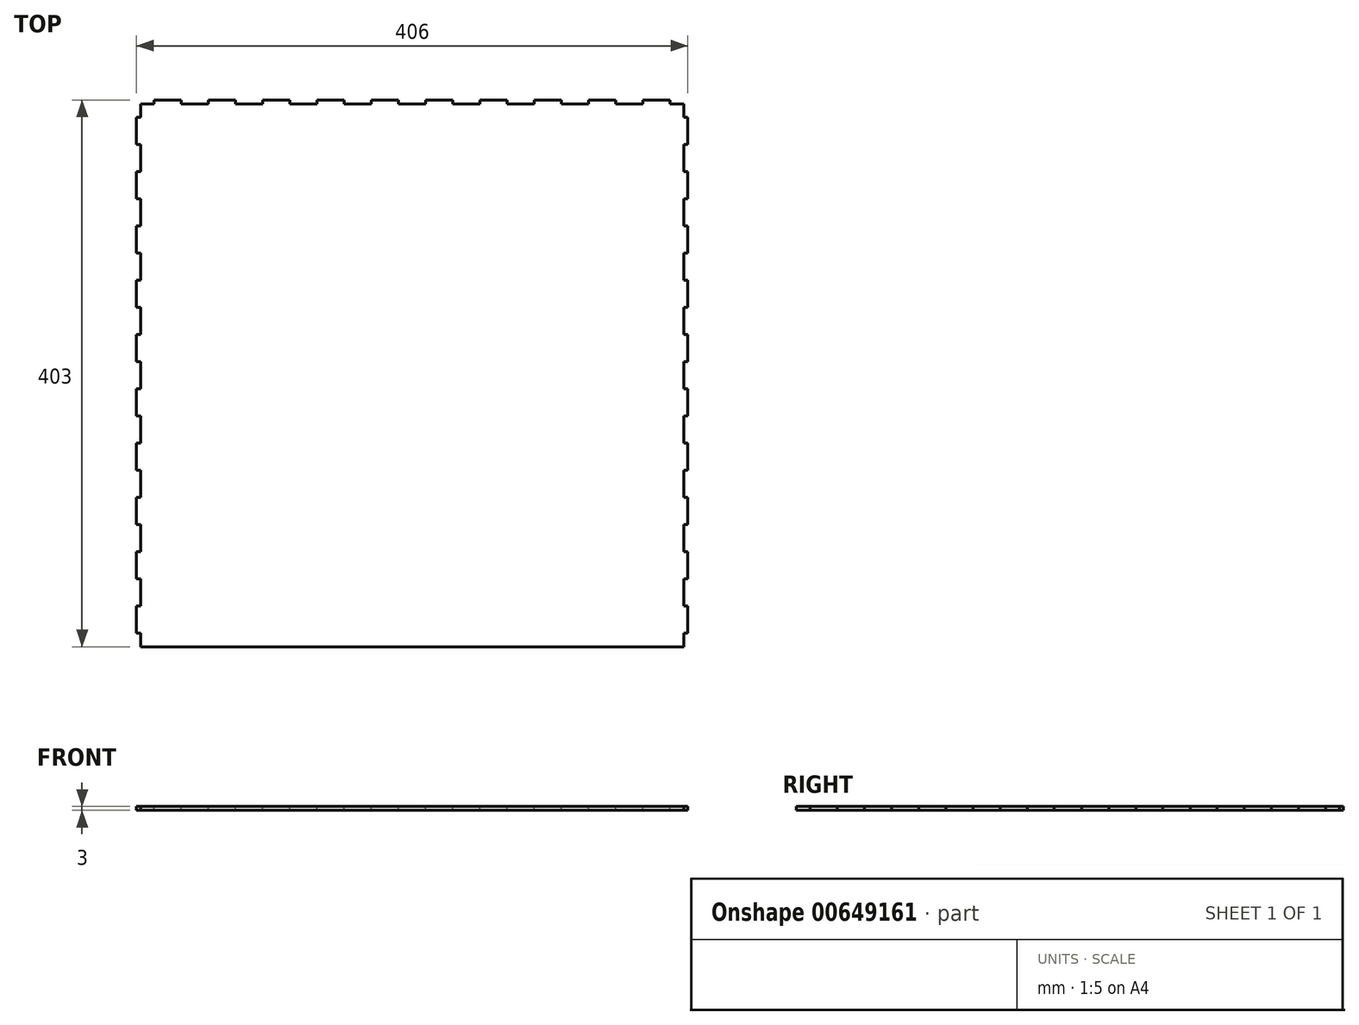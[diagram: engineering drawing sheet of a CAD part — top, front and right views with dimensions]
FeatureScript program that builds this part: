
annotation { "Feature Type Name" : "Feature", "Feature Type Description" : "" }
export const myFeature = defineFeature(function(context is Context, id is Id, definition is map)
    precondition{}
    {
        {
            var Q0;
            Q0=qCreatedBy(makeId("Top.planeOp"),FACE);
            var sketch = newSketch(context, id + "F0", { "sketchPlane" : qUnion([Q0])});
            skLineSegment(sketch, "E0.bottom", {"start": v(200, -200) * mm, "end": v(-200, -200) * mm});
            skLineSegment(sketch, "E0.top", {"start": v(200, 200) * mm, "end": v(-200, 200) * mm});
            skLineSegment(sketch, "E0.left", {"start": v(200, -200) * mm, "end": v(200, 200) * mm});
            skLineSegment(sketch, "E0.right", {"start": v(-200, -200) * mm, "end": v(-200, 200) * mm});
            skPoint(sketch, "E0.middle", {"position": v(0, 0) * mm});
            skSolve(sketch);
        }
        {
            var Q0;
            Q0=makeQuery(id+"F0.imprint","IMPRINT",FACE,{"disambiguationData":[TD([[makeQuery(id+"F0.imprint","IMPRINT",EDGE,{"derivedFrom":sQuery(id+"F0.wireOp",EDGE,"E0.bottom")}),-1.0]])]});
            extrude(context, id + "F1", {"entities" : qUnion([Q0]), "depth" : 3 * mm, "offsetDistance" : 25 * mm});
        }
        {
            var Q0;
            Q0=makeQuery(id+"F1.opExtrude","CAP_FACE",FACE,{"disambiguationData":[OSD([sQuery(id+"F0.wireOp",EDGE,"E0.bottom"),sQuery(id+"F0.wireOp",EDGE,"E0.top"),sQuery(id+"F0.wireOp",EDGE,"E0.left"),sQuery(id+"F0.wireOp",EDGE,"E0.right")])],"isStart":false});
            var sketch = newSketch(context, id + "F2", { "sketchPlane" : qUnion([Q0])});
            skLineSegment(sketch, "E1", {"start": v(-200, -200) * mm, "end": v(-190, -200) * mm, "construction": true});
            skLineSegment(sketch, "E2.bottom", {"start": v(-190, -200) * mm, "end": v(-170, -200) * mm});
            skLineSegment(sketch, "E2.top", {"start": v(-190, -203) * mm, "end": v(-170, -203) * mm});
            skLineSegment(sketch, "E2.left", {"start": v(-190, -200) * mm, "end": v(-190, -203) * mm});
            skLineSegment(sketch, "E2.right", {"start": v(-170, -200) * mm, "end": v(-170, -203) * mm});
            skLineSegment(sketch, "E3.1.0.0", {"start": v(-150, -200) * mm, "end": v(-150, -203) * mm});
            skLineSegment(sketch, "E3.1.0.1", {"start": v(-150, -200) * mm, "end": v(-130, -200) * mm});
            skLineSegment(sketch, "E3.1.0.2", {"start": v(-150, -203) * mm, "end": v(-130, -203) * mm});
            skLineSegment(sketch, "E3.1.0.3", {"start": v(-130, -200) * mm, "end": v(-130, -203) * mm});
            skLineSegment(sketch, "E3.2.0.0", {"start": v(-110, -200) * mm, "end": v(-110, -203) * mm});
            skLineSegment(sketch, "E3.2.0.1", {"start": v(-110, -200) * mm, "end": v(-90, -200) * mm});
            skLineSegment(sketch, "E3.2.0.2", {"start": v(-110, -203) * mm, "end": v(-90, -203) * mm});
            skLineSegment(sketch, "E3.2.0.3", {"start": v(-90, -200) * mm, "end": v(-90, -203) * mm});
            skLineSegment(sketch, "E3.3.0.0", {"start": v(-70, -200) * mm, "end": v(-70, -203) * mm});
            skLineSegment(sketch, "E3.3.0.1", {"start": v(-70, -200) * mm, "end": v(-50, -200) * mm});
            skLineSegment(sketch, "E3.3.0.2", {"start": v(-70, -203) * mm, "end": v(-50, -203) * mm});
            skLineSegment(sketch, "E3.3.0.3", {"start": v(-50, -200) * mm, "end": v(-50, -203) * mm});
            skLineSegment(sketch, "E3.4.0.0", {"start": v(-30, -200) * mm, "end": v(-30, -203) * mm});
            skLineSegment(sketch, "E3.4.0.1", {"start": v(-30, -200) * mm, "end": v(-10, -200) * mm});
            skLineSegment(sketch, "E3.4.0.2", {"start": v(-30, -203) * mm, "end": v(-10, -203) * mm});
            skLineSegment(sketch, "E3.4.0.3", {"start": v(-10, -200) * mm, "end": v(-10, -203) * mm});
            skLineSegment(sketch, "E3.5.0.0", {"start": v(10, -200) * mm, "end": v(10, -203) * mm});
            skLineSegment(sketch, "E3.5.0.1", {"start": v(10, -200) * mm, "end": v(30, -200) * mm});
            skLineSegment(sketch, "E3.5.0.2", {"start": v(10, -203) * mm, "end": v(30, -203) * mm});
            skLineSegment(sketch, "E3.5.0.3", {"start": v(30, -200) * mm, "end": v(30, -203) * mm});
            skLineSegment(sketch, "E3.6.0.0", {"start": v(50, -200) * mm, "end": v(50, -203) * mm});
            skLineSegment(sketch, "E3.6.0.1", {"start": v(50, -200) * mm, "end": v(70, -200) * mm});
            skLineSegment(sketch, "E3.6.0.2", {"start": v(50, -203) * mm, "end": v(70, -203) * mm});
            skLineSegment(sketch, "E3.6.0.3", {"start": v(70, -200) * mm, "end": v(70, -203) * mm});
            skLineSegment(sketch, "E3.7.0.0", {"start": v(90, -200) * mm, "end": v(90, -203) * mm});
            skLineSegment(sketch, "E3.7.0.1", {"start": v(90, -200) * mm, "end": v(110, -200) * mm});
            skLineSegment(sketch, "E3.7.0.2", {"start": v(90, -203) * mm, "end": v(110, -203) * mm});
            skLineSegment(sketch, "E3.7.0.3", {"start": v(110, -200) * mm, "end": v(110, -203) * mm});
            skLineSegment(sketch, "E3.8.0.0", {"start": v(130, -200) * mm, "end": v(130, -203) * mm});
            skLineSegment(sketch, "E3.8.0.1", {"start": v(130, -200) * mm, "end": v(150, -200) * mm});
            skLineSegment(sketch, "E3.8.0.2", {"start": v(130, -203) * mm, "end": v(150, -203) * mm});
            skLineSegment(sketch, "E3.8.0.3", {"start": v(150, -200) * mm, "end": v(150, -203) * mm});
            skLineSegment(sketch, "E3.9.0.0", {"start": v(170, -200) * mm, "end": v(170, -203) * mm});
            skLineSegment(sketch, "E3.9.0.1", {"start": v(170, -200) * mm, "end": v(190, -200) * mm});
            skLineSegment(sketch, "E3.9.0.2", {"start": v(170, -203) * mm, "end": v(190, -203) * mm});
            skLineSegment(sketch, "E3.9.0.3", {"start": v(190, -200) * mm, "end": v(190, -203) * mm});
            skLineSegment(sketch, "E3.direction1", {"start": v(-190, -203) * mm, "end": v(-150, -203) * mm, "construction": true});
            skLineSegment(sketch, "E4.1.0", {"start": v(200, 90) * mm, "end": v(200, 110) * mm});
            skLineSegment(sketch, "E4.1.1", {"start": v(200, 170) * mm, "end": v(203, 170) * mm});
            skLineSegment(sketch, "E4.1.2", {"start": v(200, 10) * mm, "end": v(203, 10) * mm});
            skLineSegment(sketch, "E4.1.3", {"start": v(200, 130) * mm, "end": v(203, 130) * mm});
            skLineSegment(sketch, "E4.1.4", {"start": v(200, -30) * mm, "end": v(203, -30) * mm});
            skLineSegment(sketch, "E4.1.5", {"start": v(203, -190) * mm, "end": v(203, -150) * mm, "construction": true});
            skLineSegment(sketch, "E4.1.6", {"start": v(200, 170) * mm, "end": v(200, 190) * mm});
            skLineSegment(sketch, "E4.1.7", {"start": v(203, 90) * mm, "end": v(203, 110) * mm});
            skLineSegment(sketch, "E4.1.8", {"start": v(200, 10) * mm, "end": v(200, 30) * mm});
            skLineSegment(sketch, "E4.1.9", {"start": v(200, 130) * mm, "end": v(200, 150) * mm});
            skLineSegment(sketch, "E4.1.10", {"start": v(200, -30) * mm, "end": v(200, -10) * mm});
            skLineSegment(sketch, "E4.1.11", {"start": v(200, 50) * mm, "end": v(200, 70) * mm});
            skLineSegment(sketch, "E4.1.12", {"start": v(200, -70) * mm, "end": v(200, -50) * mm});
            skLineSegment(sketch, "E4.1.13", {"start": v(203, -70) * mm, "end": v(203, -50) * mm});
            skLineSegment(sketch, "E4.1.14", {"start": v(200, -190) * mm, "end": v(200, -170) * mm});
            skLineSegment(sketch, "E4.1.15", {"start": v(200, -170) * mm, "end": v(203, -170) * mm});
            skLineSegment(sketch, "E4.1.16", {"start": v(203, 130) * mm, "end": v(203, 150) * mm});
            skLineSegment(sketch, "E4.1.17", {"start": v(203, -30) * mm, "end": v(203, -10) * mm});
            skLineSegment(sketch, "E4.1.18", {"start": v(200, -150) * mm, "end": v(200, -130) * mm});
            skLineSegment(sketch, "E4.1.19", {"start": v(203, -150) * mm, "end": v(203, -130) * mm});
            skLineSegment(sketch, "E4.1.20", {"start": v(200, -130) * mm, "end": v(203, -130) * mm});
            skLineSegment(sketch, "E4.1.21", {"start": v(200, -110) * mm, "end": v(200, -90) * mm});
            skLineSegment(sketch, "E4.1.22", {"start": v(203, -110) * mm, "end": v(203, -90) * mm});
            skLineSegment(sketch, "E4.1.23", {"start": v(200, -90) * mm, "end": v(203, -90) * mm});
            skLineSegment(sketch, "E4.1.24", {"start": v(200, 110) * mm, "end": v(203, 110) * mm});
            skLineSegment(sketch, "E4.1.25", {"start": v(200, -50) * mm, "end": v(203, -50) * mm});
            skLineSegment(sketch, "E4.1.26", {"start": v(203, 50) * mm, "end": v(203, 70) * mm});
            skLineSegment(sketch, "E4.1.27", {"start": v(203, 170) * mm, "end": v(203, 190) * mm});
            skLineSegment(sketch, "E4.1.28", {"start": v(203, 10) * mm, "end": v(203, 30) * mm});
            skLineSegment(sketch, "E4.1.29", {"start": v(200, 150) * mm, "end": v(203, 150) * mm});
            skLineSegment(sketch, "E4.1.30", {"start": v(200, -10) * mm, "end": v(203, -10) * mm});
            skLineSegment(sketch, "E4.1.31", {"start": v(200, 90) * mm, "end": v(203, 90) * mm});
            skLineSegment(sketch, "E4.1.32", {"start": v(200, 70) * mm, "end": v(203, 70) * mm});
            skLineSegment(sketch, "E4.1.33", {"start": v(200, 190) * mm, "end": v(203, 190) * mm});
            skLineSegment(sketch, "E4.1.34", {"start": v(200, 30) * mm, "end": v(203, 30) * mm});
            skLineSegment(sketch, "E4.1.35", {"start": v(200, 50) * mm, "end": v(203, 50) * mm});
            skLineSegment(sketch, "E4.1.36", {"start": v(200, -70) * mm, "end": v(203, -70) * mm});
            skLineSegment(sketch, "E4.1.37", {"start": v(203, -190) * mm, "end": v(203, -170) * mm});
            skLineSegment(sketch, "E4.1.38", {"start": v(200, -150) * mm, "end": v(203, -150) * mm});
            skLineSegment(sketch, "E4.1.39", {"start": v(200, -110) * mm, "end": v(203, -110) * mm});
            skLineSegment(sketch, "E4.1.40", {"start": v(200, -200) * mm, "end": v(200, -190) * mm, "construction": true});
            skLineSegment(sketch, "E4.1.41", {"start": v(200, -190) * mm, "end": v(203, -190) * mm});
            skLineSegment(sketch, "E4.2.0", {"start": v(-90, 200) * mm, "end": v(-110, 200) * mm});
            skLineSegment(sketch, "E4.2.1", {"start": v(-170, 200) * mm, "end": v(-170, 203) * mm});
            skLineSegment(sketch, "E4.2.2", {"start": v(-10, 200) * mm, "end": v(-10, 203) * mm});
            skLineSegment(sketch, "E4.2.3", {"start": v(-130, 200) * mm, "end": v(-130, 203) * mm});
            skLineSegment(sketch, "E4.2.4", {"start": v(30, 200) * mm, "end": v(30, 203) * mm});
            skLineSegment(sketch, "E4.2.5", {"start": v(190, 203) * mm, "end": v(150, 203) * mm, "construction": true});
            skLineSegment(sketch, "E4.2.6", {"start": v(-170, 200) * mm, "end": v(-190, 200) * mm});
            skLineSegment(sketch, "E4.2.7", {"start": v(-90, 203) * mm, "end": v(-110, 203) * mm});
            skLineSegment(sketch, "E4.2.8", {"start": v(-10, 200) * mm, "end": v(-30, 200) * mm});
            skLineSegment(sketch, "E4.2.9", {"start": v(-130, 200) * mm, "end": v(-150, 200) * mm});
            skLineSegment(sketch, "E4.2.10", {"start": v(30, 200) * mm, "end": v(10, 200) * mm});
            skLineSegment(sketch, "E4.2.11", {"start": v(-50, 200) * mm, "end": v(-70, 200) * mm});
            skLineSegment(sketch, "E4.2.12", {"start": v(70, 200) * mm, "end": v(50, 200) * mm});
            skLineSegment(sketch, "E4.2.13", {"start": v(70, 203) * mm, "end": v(50, 203) * mm});
            skLineSegment(sketch, "E4.2.14", {"start": v(190, 200) * mm, "end": v(170, 200) * mm});
            skLineSegment(sketch, "E4.2.15", {"start": v(170, 200) * mm, "end": v(170, 203) * mm});
            skLineSegment(sketch, "E4.2.16", {"start": v(-130, 203) * mm, "end": v(-150, 203) * mm});
            skLineSegment(sketch, "E4.2.17", {"start": v(30, 203) * mm, "end": v(10, 203) * mm});
            skLineSegment(sketch, "E4.2.18", {"start": v(150, 200) * mm, "end": v(130, 200) * mm});
            skLineSegment(sketch, "E4.2.19", {"start": v(150, 203) * mm, "end": v(130, 203) * mm});
            skLineSegment(sketch, "E4.2.20", {"start": v(130, 200) * mm, "end": v(130, 203) * mm});
            skLineSegment(sketch, "E4.2.21", {"start": v(110, 200) * mm, "end": v(90, 200) * mm});
            skLineSegment(sketch, "E4.2.22", {"start": v(110, 203) * mm, "end": v(90, 203) * mm});
            skLineSegment(sketch, "E4.2.23", {"start": v(90, 200) * mm, "end": v(90, 203) * mm});
            skLineSegment(sketch, "E4.2.24", {"start": v(-110, 200) * mm, "end": v(-110, 203) * mm});
            skLineSegment(sketch, "E4.2.25", {"start": v(50, 200) * mm, "end": v(50, 203) * mm});
            skLineSegment(sketch, "E4.2.26", {"start": v(-50, 203) * mm, "end": v(-70, 203) * mm});
            skLineSegment(sketch, "E4.2.27", {"start": v(-170, 203) * mm, "end": v(-190, 203) * mm});
            skLineSegment(sketch, "E4.2.28", {"start": v(-10, 203) * mm, "end": v(-30, 203) * mm});
            skLineSegment(sketch, "E4.2.29", {"start": v(-150, 200) * mm, "end": v(-150, 203) * mm});
            skLineSegment(sketch, "E4.2.30", {"start": v(10, 200) * mm, "end": v(10, 203) * mm});
            skLineSegment(sketch, "E4.2.31", {"start": v(-90, 200) * mm, "end": v(-90, 203) * mm});
            skLineSegment(sketch, "E4.2.32", {"start": v(-70, 200) * mm, "end": v(-70, 203) * mm});
            skLineSegment(sketch, "E4.2.33", {"start": v(-190, 200) * mm, "end": v(-190, 203) * mm});
            skLineSegment(sketch, "E4.2.34", {"start": v(-30, 200) * mm, "end": v(-30, 203) * mm});
            skLineSegment(sketch, "E4.2.35", {"start": v(-50, 200) * mm, "end": v(-50, 203) * mm});
            skLineSegment(sketch, "E4.2.36", {"start": v(70, 200) * mm, "end": v(70, 203) * mm});
            skLineSegment(sketch, "E4.2.37", {"start": v(190, 203) * mm, "end": v(170, 203) * mm});
            skLineSegment(sketch, "E4.2.38", {"start": v(150, 200) * mm, "end": v(150, 203) * mm});
            skLineSegment(sketch, "E4.2.39", {"start": v(110, 200) * mm, "end": v(110, 203) * mm});
            skLineSegment(sketch, "E4.2.40", {"start": v(200, 200) * mm, "end": v(190, 200) * mm, "construction": true});
            skLineSegment(sketch, "E4.2.41", {"start": v(190, 200) * mm, "end": v(190, 203) * mm});
            skLineSegment(sketch, "E4.3.0", {"start": v(-200, -90) * mm, "end": v(-200, -110) * mm});
            skLineSegment(sketch, "E4.3.1", {"start": v(-200, -170) * mm, "end": v(-203, -170) * mm});
            skLineSegment(sketch, "E4.3.2", {"start": v(-200, -10) * mm, "end": v(-203, -10) * mm});
            skLineSegment(sketch, "E4.3.3", {"start": v(-200, -130) * mm, "end": v(-203, -130) * mm});
            skLineSegment(sketch, "E4.3.4", {"start": v(-200, 30) * mm, "end": v(-203, 30) * mm});
            skLineSegment(sketch, "E4.3.5", {"start": v(-203, 190) * mm, "end": v(-203, 150) * mm, "construction": true});
            skLineSegment(sketch, "E4.3.6", {"start": v(-200, -170) * mm, "end": v(-200, -190) * mm});
            skLineSegment(sketch, "E4.3.7", {"start": v(-203, -90) * mm, "end": v(-203, -110) * mm});
            skLineSegment(sketch, "E4.3.8", {"start": v(-200, -10) * mm, "end": v(-200, -30) * mm});
            skLineSegment(sketch, "E4.3.9", {"start": v(-200, -130) * mm, "end": v(-200, -150) * mm});
            skLineSegment(sketch, "E4.3.10", {"start": v(-200, 30) * mm, "end": v(-200, 10) * mm});
            skLineSegment(sketch, "E4.3.11", {"start": v(-200, -50) * mm, "end": v(-200, -70) * mm});
            skLineSegment(sketch, "E4.3.12", {"start": v(-200, 70) * mm, "end": v(-200, 50) * mm});
            skLineSegment(sketch, "E4.3.13", {"start": v(-203, 70) * mm, "end": v(-203, 50) * mm});
            skLineSegment(sketch, "E4.3.14", {"start": v(-200, 190) * mm, "end": v(-200, 170) * mm});
            skLineSegment(sketch, "E4.3.15", {"start": v(-200, 170) * mm, "end": v(-203, 170) * mm});
            skLineSegment(sketch, "E4.3.16", {"start": v(-203, -130) * mm, "end": v(-203, -150) * mm});
            skLineSegment(sketch, "E4.3.17", {"start": v(-203, 30) * mm, "end": v(-203, 10) * mm});
            skLineSegment(sketch, "E4.3.18", {"start": v(-200, 150) * mm, "end": v(-200, 130) * mm});
            skLineSegment(sketch, "E4.3.19", {"start": v(-203, 150) * mm, "end": v(-203, 130) * mm});
            skLineSegment(sketch, "E4.3.20", {"start": v(-200, 130) * mm, "end": v(-203, 130) * mm});
            skLineSegment(sketch, "E4.3.21", {"start": v(-200, 110) * mm, "end": v(-200, 90) * mm});
            skLineSegment(sketch, "E4.3.22", {"start": v(-203, 110) * mm, "end": v(-203, 90) * mm});
            skLineSegment(sketch, "E4.3.23", {"start": v(-200, 90) * mm, "end": v(-203, 90) * mm});
            skLineSegment(sketch, "E4.3.24", {"start": v(-200, -110) * mm, "end": v(-203, -110) * mm});
            skLineSegment(sketch, "E4.3.25", {"start": v(-200, 50) * mm, "end": v(-203, 50) * mm});
            skLineSegment(sketch, "E4.3.26", {"start": v(-203, -50) * mm, "end": v(-203, -70) * mm});
            skLineSegment(sketch, "E4.3.27", {"start": v(-203, -170) * mm, "end": v(-203, -190) * mm});
            skLineSegment(sketch, "E4.3.28", {"start": v(-203, -10) * mm, "end": v(-203, -30) * mm});
            skLineSegment(sketch, "E4.3.29", {"start": v(-200, -150) * mm, "end": v(-203, -150) * mm});
            skLineSegment(sketch, "E4.3.30", {"start": v(-200, 10) * mm, "end": v(-203, 10) * mm});
            skLineSegment(sketch, "E4.3.31", {"start": v(-200, -90) * mm, "end": v(-203, -90) * mm});
            skLineSegment(sketch, "E4.3.32", {"start": v(-200, -70) * mm, "end": v(-203, -70) * mm});
            skLineSegment(sketch, "E4.3.33", {"start": v(-200, -190) * mm, "end": v(-203, -190) * mm});
            skLineSegment(sketch, "E4.3.34", {"start": v(-200, -30) * mm, "end": v(-203, -30) * mm});
            skLineSegment(sketch, "E4.3.35", {"start": v(-200, -50) * mm, "end": v(-203, -50) * mm});
            skLineSegment(sketch, "E4.3.36", {"start": v(-200, 70) * mm, "end": v(-203, 70) * mm});
            skLineSegment(sketch, "E4.3.37", {"start": v(-203, 190) * mm, "end": v(-203, 170) * mm});
            skLineSegment(sketch, "E4.3.38", {"start": v(-200, 150) * mm, "end": v(-203, 150) * mm});
            skLineSegment(sketch, "E4.3.39", {"start": v(-200, 110) * mm, "end": v(-203, 110) * mm});
            skLineSegment(sketch, "E4.3.40", {"start": v(-200, 200) * mm, "end": v(-200, 190) * mm, "construction": true});
            skLineSegment(sketch, "E4.3.41", {"start": v(-200, 190) * mm, "end": v(-203, 190) * mm});
            skPoint(sketch, "E4.center", {"position": v(0, 0) * mm});
            skSolve(sketch);
        }
        {
            var Q0;
            Q0=qSketchRegion(id+"F2",true);
            var Q1;
            Q1=makeQuery(id+"F1.opExtrude","CAP_FACE",FACE,{"disambiguationData":[OSD([sQuery(id+"F0.wireOp",EDGE,"E0.bottom"),sQuery(id+"F0.wireOp",EDGE,"E0.top"),sQuery(id+"F0.wireOp",EDGE,"E0.left"),sQuery(id+"F0.wireOp",EDGE,"E0.right")])],"isStart":true});
            extrude(context, id + "F3", {"entities" : qUnion([Q0]), "operationType" : NewBodyOperationType.ADD, "endBound" : BoundingType.UP_TO_SURFACE, "oppositeDirection" : true, "depth" : 25 * mm, "endBoundEntityFace" : qUnion([Q1]), "offsetDistance" : 25 * mm});
        }
        {
            var Q0;
            Q0=makeQuery(id+"F3.boolean.opBoolean","MERGE",FACE,{"derivedFrom":[makeQuery(id+"F1.opExtrude","CAP_FACE",FACE,{"disambiguationData":[OSD([sQuery(id+"F0.wireOp",EDGE,"E0.bottom"),sQuery(id+"F0.wireOp",EDGE,"E0.top"),sQuery(id+"F0.wireOp",EDGE,"E0.left"),sQuery(id+"F0.wireOp",EDGE,"E0.right")])],"isStart":false}),makeQuery(id+"F3.opExtrude","CAP_FACE",FACE,{"disambiguationData":[OSD([sQuery(id+"F2.wireOp",EDGE,"E2.bottom"),sQuery(id+"F2.wireOp",EDGE,"E2.top"),sQuery(id+"F2.wireOp",EDGE,"E2.left"),sQuery(id+"F2.wireOp",EDGE,"E2.right")])],"isStart":true}),makeQuery(id+"F3.opExtrude","CAP_FACE",FACE,{"disambiguationData":[OSD([sQuery(id+"F2.wireOp",EDGE,"E3.1.0.0"),sQuery(id+"F2.wireOp",EDGE,"E3.1.0.1"),sQuery(id+"F2.wireOp",EDGE,"E3.1.0.2"),sQuery(id+"F2.wireOp",EDGE,"E3.1.0.3")])],"isStart":true}),makeQuery(id+"F3.opExtrude","CAP_FACE",FACE,{"disambiguationData":[OSD([sQuery(id+"F2.wireOp",EDGE,"E3.2.0.0"),sQuery(id+"F2.wireOp",EDGE,"E3.2.0.1"),sQuery(id+"F2.wireOp",EDGE,"E3.2.0.2"),sQuery(id+"F2.wireOp",EDGE,"E3.2.0.3")])],"isStart":true}),makeQuery(id+"F3.opExtrude","CAP_FACE",FACE,{"disambiguationData":[OSD([sQuery(id+"F2.wireOp",EDGE,"E3.3.0.0"),sQuery(id+"F2.wireOp",EDGE,"E3.3.0.1"),sQuery(id+"F2.wireOp",EDGE,"E3.3.0.2"),sQuery(id+"F2.wireOp",EDGE,"E3.3.0.3")])],"isStart":true}),makeQuery(id+"F3.opExtrude","CAP_FACE",FACE,{"disambiguationData":[OSD([sQuery(id+"F2.wireOp",EDGE,"E3.4.0.0"),sQuery(id+"F2.wireOp",EDGE,"E3.4.0.1"),sQuery(id+"F2.wireOp",EDGE,"E3.4.0.2"),sQuery(id+"F2.wireOp",EDGE,"E3.4.0.3")])],"isStart":true}),makeQuery(id+"F3.opExtrude","CAP_FACE",FACE,{"disambiguationData":[OSD([sQuery(id+"F2.wireOp",EDGE,"E3.5.0.0"),sQuery(id+"F2.wireOp",EDGE,"E3.5.0.1"),sQuery(id+"F2.wireOp",EDGE,"E3.5.0.2"),sQuery(id+"F2.wireOp",EDGE,"E3.5.0.3")])],"isStart":true}),makeQuery(id+"F3.opExtrude","CAP_FACE",FACE,{"disambiguationData":[OSD([sQuery(id+"F2.wireOp",EDGE,"E3.6.0.0"),sQuery(id+"F2.wireOp",EDGE,"E3.6.0.1"),sQuery(id+"F2.wireOp",EDGE,"E3.6.0.2"),sQuery(id+"F2.wireOp",EDGE,"E3.6.0.3")])],"isStart":true}),makeQuery(id+"F3.opExtrude","CAP_FACE",FACE,{"disambiguationData":[OSD([sQuery(id+"F2.wireOp",EDGE,"E3.7.0.0"),sQuery(id+"F2.wireOp",EDGE,"E3.7.0.1"),sQuery(id+"F2.wireOp",EDGE,"E3.7.0.2"),sQuery(id+"F2.wireOp",EDGE,"E3.7.0.3")])],"isStart":true}),makeQuery(id+"F3.opExtrude","CAP_FACE",FACE,{"disambiguationData":[OSD([sQuery(id+"F2.wireOp",EDGE,"E3.8.0.0"),sQuery(id+"F2.wireOp",EDGE,"E3.8.0.1"),sQuery(id+"F2.wireOp",EDGE,"E3.8.0.2"),sQuery(id+"F2.wireOp",EDGE,"E3.8.0.3")])],"isStart":true}),makeQuery(id+"F3.opExtrude","CAP_FACE",FACE,{"disambiguationData":[OSD([sQuery(id+"F2.wireOp",EDGE,"E3.9.0.0"),sQuery(id+"F2.wireOp",EDGE,"E3.9.0.1"),sQuery(id+"F2.wireOp",EDGE,"E3.9.0.2"),sQuery(id+"F2.wireOp",EDGE,"E3.9.0.3")])],"isStart":true}),makeQuery(id+"F3.opExtrude","CAP_FACE",FACE,{"disambiguationData":[OSD([sQuery(id+"F2.wireOp",EDGE,"E4.1.0"),sQuery(id+"F2.wireOp",EDGE,"E4.1.7"),sQuery(id+"F2.wireOp",EDGE,"E4.1.24"),sQuery(id+"F2.wireOp",EDGE,"E4.1.31")])],"isStart":true}),makeQuery(id+"F3.opExtrude","CAP_FACE",FACE,{"disambiguationData":[OSD([sQuery(id+"F2.wireOp",EDGE,"E4.1.1"),sQuery(id+"F2.wireOp",EDGE,"E4.1.6"),sQuery(id+"F2.wireOp",EDGE,"E4.1.27"),sQuery(id+"F2.wireOp",EDGE,"E4.1.33")])],"isStart":true}),makeQuery(id+"F3.opExtrude","CAP_FACE",FACE,{"disambiguationData":[OSD([sQuery(id+"F2.wireOp",EDGE,"E4.1.2"),sQuery(id+"F2.wireOp",EDGE,"E4.1.8"),sQuery(id+"F2.wireOp",EDGE,"E4.1.28"),sQuery(id+"F2.wireOp",EDGE,"E4.1.34")])],"isStart":true}),makeQuery(id+"F3.opExtrude","CAP_FACE",FACE,{"disambiguationData":[OSD([sQuery(id+"F2.wireOp",EDGE,"E4.1.3"),sQuery(id+"F2.wireOp",EDGE,"E4.1.9"),sQuery(id+"F2.wireOp",EDGE,"E4.1.16"),sQuery(id+"F2.wireOp",EDGE,"E4.1.29")])],"isStart":true}),makeQuery(id+"F3.opExtrude","CAP_FACE",FACE,{"disambiguationData":[OSD([sQuery(id+"F2.wireOp",EDGE,"E4.1.4"),sQuery(id+"F2.wireOp",EDGE,"E4.1.10"),sQuery(id+"F2.wireOp",EDGE,"E4.1.17"),sQuery(id+"F2.wireOp",EDGE,"E4.1.30")])],"isStart":true}),makeQuery(id+"F3.opExtrude","CAP_FACE",FACE,{"disambiguationData":[OSD([sQuery(id+"F2.wireOp",EDGE,"E4.1.11"),sQuery(id+"F2.wireOp",EDGE,"E4.1.26"),sQuery(id+"F2.wireOp",EDGE,"E4.1.32"),sQuery(id+"F2.wireOp",EDGE,"E4.1.35")])],"isStart":true}),makeQuery(id+"F3.opExtrude","CAP_FACE",FACE,{"disambiguationData":[OSD([sQuery(id+"F2.wireOp",EDGE,"E4.1.12"),sQuery(id+"F2.wireOp",EDGE,"E4.1.13"),sQuery(id+"F2.wireOp",EDGE,"E4.1.25"),sQuery(id+"F2.wireOp",EDGE,"E4.1.36")])],"isStart":true}),makeQuery(id+"F3.opExtrude","CAP_FACE",FACE,{"disambiguationData":[OSD([sQuery(id+"F2.wireOp",EDGE,"E4.1.14"),sQuery(id+"F2.wireOp",EDGE,"E4.1.15"),sQuery(id+"F2.wireOp",EDGE,"E4.1.37"),sQuery(id+"F2.wireOp",EDGE,"E4.1.41")])],"isStart":true}),makeQuery(id+"F3.opExtrude","CAP_FACE",FACE,{"disambiguationData":[OSD([sQuery(id+"F2.wireOp",EDGE,"E4.1.18"),sQuery(id+"F2.wireOp",EDGE,"E4.1.19"),sQuery(id+"F2.wireOp",EDGE,"E4.1.20"),sQuery(id+"F2.wireOp",EDGE,"E4.1.38")])],"isStart":true}),makeQuery(id+"F3.opExtrude","CAP_FACE",FACE,{"disambiguationData":[OSD([sQuery(id+"F2.wireOp",EDGE,"E4.1.21"),sQuery(id+"F2.wireOp",EDGE,"E4.1.22"),sQuery(id+"F2.wireOp",EDGE,"E4.1.23"),sQuery(id+"F2.wireOp",EDGE,"E4.1.39")])],"isStart":true}),makeQuery(id+"F3.opExtrude","CAP_FACE",FACE,{"disambiguationData":[OSD([sQuery(id+"F2.wireOp",EDGE,"E4.2.0"),sQuery(id+"F2.wireOp",EDGE,"E4.2.7"),sQuery(id+"F2.wireOp",EDGE,"E4.2.24"),sQuery(id+"F2.wireOp",EDGE,"E4.2.31")])],"isStart":true}),makeQuery(id+"F3.opExtrude","CAP_FACE",FACE,{"disambiguationData":[OSD([sQuery(id+"F2.wireOp",EDGE,"E4.2.1"),sQuery(id+"F2.wireOp",EDGE,"E4.2.6"),sQuery(id+"F2.wireOp",EDGE,"E4.2.27"),sQuery(id+"F2.wireOp",EDGE,"E4.2.33")])],"isStart":true}),makeQuery(id+"F3.opExtrude","CAP_FACE",FACE,{"disambiguationData":[OSD([sQuery(id+"F2.wireOp",EDGE,"E4.2.2"),sQuery(id+"F2.wireOp",EDGE,"E4.2.8"),sQuery(id+"F2.wireOp",EDGE,"E4.2.28"),sQuery(id+"F2.wireOp",EDGE,"E4.2.34")])],"isStart":true}),makeQuery(id+"F3.opExtrude","CAP_FACE",FACE,{"disambiguationData":[OSD([sQuery(id+"F2.wireOp",EDGE,"E4.2.3"),sQuery(id+"F2.wireOp",EDGE,"E4.2.9"),sQuery(id+"F2.wireOp",EDGE,"E4.2.16"),sQuery(id+"F2.wireOp",EDGE,"E4.2.29")])],"isStart":true}),makeQuery(id+"F3.opExtrude","CAP_FACE",FACE,{"disambiguationData":[OSD([sQuery(id+"F2.wireOp",EDGE,"E4.2.4"),sQuery(id+"F2.wireOp",EDGE,"E4.2.10"),sQuery(id+"F2.wireOp",EDGE,"E4.2.17"),sQuery(id+"F2.wireOp",EDGE,"E4.2.30")])],"isStart":true}),makeQuery(id+"F3.opExtrude","CAP_FACE",FACE,{"disambiguationData":[OSD([sQuery(id+"F2.wireOp",EDGE,"E4.2.11"),sQuery(id+"F2.wireOp",EDGE,"E4.2.26"),sQuery(id+"F2.wireOp",EDGE,"E4.2.32"),sQuery(id+"F2.wireOp",EDGE,"E4.2.35")])],"isStart":true}),makeQuery(id+"F3.opExtrude","CAP_FACE",FACE,{"disambiguationData":[OSD([sQuery(id+"F2.wireOp",EDGE,"E4.2.12"),sQuery(id+"F2.wireOp",EDGE,"E4.2.13"),sQuery(id+"F2.wireOp",EDGE,"E4.2.25"),sQuery(id+"F2.wireOp",EDGE,"E4.2.36")])],"isStart":true}),makeQuery(id+"F3.opExtrude","CAP_FACE",FACE,{"disambiguationData":[OSD([sQuery(id+"F2.wireOp",EDGE,"E4.2.14"),sQuery(id+"F2.wireOp",EDGE,"E4.2.15"),sQuery(id+"F2.wireOp",EDGE,"E4.2.37"),sQuery(id+"F2.wireOp",EDGE,"E4.2.41")])],"isStart":true}),makeQuery(id+"F3.opExtrude","CAP_FACE",FACE,{"disambiguationData":[OSD([sQuery(id+"F2.wireOp",EDGE,"E4.2.18"),sQuery(id+"F2.wireOp",EDGE,"E4.2.19"),sQuery(id+"F2.wireOp",EDGE,"E4.2.20"),sQuery(id+"F2.wireOp",EDGE,"E4.2.38")])],"isStart":true}),makeQuery(id+"F3.opExtrude","CAP_FACE",FACE,{"disambiguationData":[OSD([sQuery(id+"F2.wireOp",EDGE,"E4.2.21"),sQuery(id+"F2.wireOp",EDGE,"E4.2.22"),sQuery(id+"F2.wireOp",EDGE,"E4.2.23"),sQuery(id+"F2.wireOp",EDGE,"E4.2.39")])],"isStart":true}),makeQuery(id+"F3.opExtrude","CAP_FACE",FACE,{"disambiguationData":[OSD([sQuery(id+"F2.wireOp",EDGE,"E4.3.0"),sQuery(id+"F2.wireOp",EDGE,"E4.3.7"),sQuery(id+"F2.wireOp",EDGE,"E4.3.24"),sQuery(id+"F2.wireOp",EDGE,"E4.3.31")])],"isStart":true}),makeQuery(id+"F3.opExtrude","CAP_FACE",FACE,{"disambiguationData":[OSD([sQuery(id+"F2.wireOp",EDGE,"E4.3.1"),sQuery(id+"F2.wireOp",EDGE,"E4.3.6"),sQuery(id+"F2.wireOp",EDGE,"E4.3.27"),sQuery(id+"F2.wireOp",EDGE,"E4.3.33")])],"isStart":true}),makeQuery(id+"F3.opExtrude","CAP_FACE",FACE,{"disambiguationData":[OSD([sQuery(id+"F2.wireOp",EDGE,"E4.3.2"),sQuery(id+"F2.wireOp",EDGE,"E4.3.8"),sQuery(id+"F2.wireOp",EDGE,"E4.3.28"),sQuery(id+"F2.wireOp",EDGE,"E4.3.34")])],"isStart":true}),makeQuery(id+"F3.opExtrude","CAP_FACE",FACE,{"disambiguationData":[OSD([sQuery(id+"F2.wireOp",EDGE,"E4.3.3"),sQuery(id+"F2.wireOp",EDGE,"E4.3.9"),sQuery(id+"F2.wireOp",EDGE,"E4.3.16"),sQuery(id+"F2.wireOp",EDGE,"E4.3.29")])],"isStart":true}),makeQuery(id+"F3.opExtrude","CAP_FACE",FACE,{"disambiguationData":[OSD([sQuery(id+"F2.wireOp",EDGE,"E4.3.4"),sQuery(id+"F2.wireOp",EDGE,"E4.3.10"),sQuery(id+"F2.wireOp",EDGE,"E4.3.17"),sQuery(id+"F2.wireOp",EDGE,"E4.3.30")])],"isStart":true}),makeQuery(id+"F3.opExtrude","CAP_FACE",FACE,{"disambiguationData":[OSD([sQuery(id+"F2.wireOp",EDGE,"E4.3.11"),sQuery(id+"F2.wireOp",EDGE,"E4.3.26"),sQuery(id+"F2.wireOp",EDGE,"E4.3.32"),sQuery(id+"F2.wireOp",EDGE,"E4.3.35")])],"isStart":true}),makeQuery(id+"F3.opExtrude","CAP_FACE",FACE,{"disambiguationData":[OSD([sQuery(id+"F2.wireOp",EDGE,"E4.3.12"),sQuery(id+"F2.wireOp",EDGE,"E4.3.13"),sQuery(id+"F2.wireOp",EDGE,"E4.3.25"),sQuery(id+"F2.wireOp",EDGE,"E4.3.36")])],"isStart":true}),makeQuery(id+"F3.opExtrude","CAP_FACE",FACE,{"disambiguationData":[OSD([sQuery(id+"F2.wireOp",EDGE,"E4.3.14"),sQuery(id+"F2.wireOp",EDGE,"E4.3.15"),sQuery(id+"F2.wireOp",EDGE,"E4.3.37"),sQuery(id+"F2.wireOp",EDGE,"E4.3.41")])],"isStart":true}),makeQuery(id+"F3.opExtrude","CAP_FACE",FACE,{"disambiguationData":[OSD([sQuery(id+"F2.wireOp",EDGE,"E4.3.18"),sQuery(id+"F2.wireOp",EDGE,"E4.3.19"),sQuery(id+"F2.wireOp",EDGE,"E4.3.20"),sQuery(id+"F2.wireOp",EDGE,"E4.3.38")])],"isStart":true}),makeQuery(id+"F3.opExtrude","CAP_FACE",FACE,{"disambiguationData":[OSD([sQuery(id+"F2.wireOp",EDGE,"E4.3.21"),sQuery(id+"F2.wireOp",EDGE,"E4.3.22"),sQuery(id+"F2.wireOp",EDGE,"E4.3.23"),sQuery(id+"F2.wireOp",EDGE,"E4.3.39")])],"isStart":true})]});
            var sketch = newSketch(context, id + "F4", { "sketchPlane" : qUnion([Q0])});
            skLineSegment(sketch, "E5.bottom", {"start": v(-190, -200) * mm, "end": v(190, -200) * mm});
            skLineSegment(sketch, "E5.top", {"start": v(-190, -203) * mm, "end": v(190, -203) * mm});
            skLineSegment(sketch, "E5.left", {"start": v(-190, -200) * mm, "end": v(-190, -203) * mm});
            skLineSegment(sketch, "E5.right", {"start": v(190, -200) * mm, "end": v(190, -203) * mm});
            skSolve(sketch);
        }
        {
            var Q0;
            Q0 = qSketchRegion(id + "F4", true);
            extrude(context, id + "F5", {"entities" : qUnion([Q0]), "operationType" : NewBodyOperationType.REMOVE, "oppositeDirection" : true, "depth" : 25 * mm, "offsetDistance" : 25 * mm});
        }
    });
